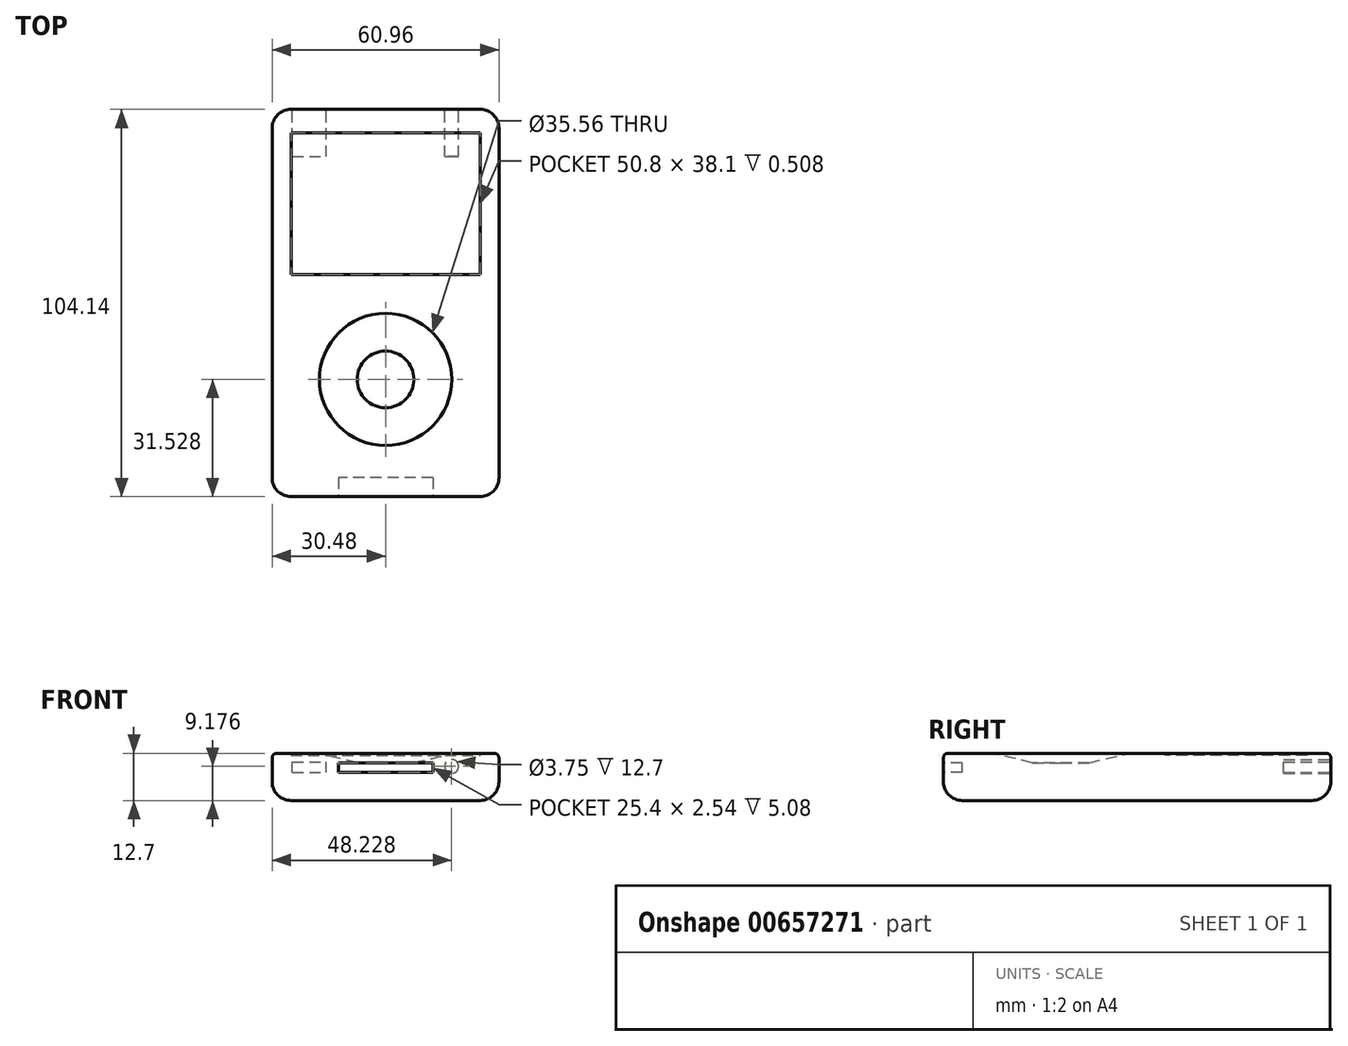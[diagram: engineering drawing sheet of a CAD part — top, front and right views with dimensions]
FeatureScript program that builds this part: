
annotation { "Feature Type Name" : "Feature", "Feature Type Description" : "" }
export const myFeature = defineFeature(function(context is Context, id is Id, definition is map)
    precondition{}
    {
        {
            var Q0;
            Q0=qCreatedBy(makeId("Top.planeOp"),FACE);
            var sketch = newSketch(context, id + "F0", { "sketchPlane" : qUnion([Q0])});
            skLineSegment(sketch, "E0.bottom", {"start": v(30.48, -52.07) * mm, "end": v(-30.48, -52.07) * mm});
            skLineSegment(sketch, "E0.top", {"start": v(30.48, 52.07) * mm, "end": v(-30.48, 52.07) * mm});
            skLineSegment(sketch, "E0.left", {"start": v(30.48, -52.07) * mm, "end": v(30.48, 52.07) * mm});
            skLineSegment(sketch, "E0.right", {"start": v(-30.48, -52.07) * mm, "end": v(-30.48, 52.07) * mm});
            skPoint(sketch, "E0.middle", {"position": v(0, 0) * mm});
            skCircle(sketch, "E1", {"center": v(0, -21.59) * mm, "radius": 17.78 * mm});
            skCircle(sketch, "E2", {"center": v(0, -21.59) * mm, "radius": 7.62 * mm});
            skLineSegment(sketch, "E3.bottom", {"start": v(-25.4, 45.72) * mm, "end": v(25.4, 45.72) * mm});
            skLineSegment(sketch, "E3.top", {"start": v(-25.4, 7.62) * mm, "end": v(25.4, 7.62) * mm});
            skLineSegment(sketch, "E3.left", {"start": v(-25.4, 45.72) * mm, "end": v(-25.4, 7.62) * mm});
            skLineSegment(sketch, "E3.right", {"start": v(25.4, 45.72) * mm, "end": v(25.4, 7.62) * mm});
            skPoint(sketch, "E3.middle", {"position": v(0, 26.67) * mm});
            skLineSegment(sketch, "E4", {"start": v(-30.48, -21.56) * mm, "end": v(30.48, -21.56) * mm, "construction": true});
            skSolve(sketch);
        }
        {
            var Q0;
            Q0=sQuery(id+"F0.wireOp",EDGE,"E0.bottom");
            cPlane(context, id + "F1", {"entities" : qUnion([Q0]), "cplaneType" : CPlaneType.LINE_ANGLE, "offset" : 25.4 * mm, "angle" : 0 * degree, "width" : 152.4 * mm, "height" : 152.4 * mm});
        }
        {
            var Q0;
            Q0=sQuery(id+"F0.wireOp",EDGE,"E0.top");
            cPlane(context, id + "F2", {"entities" : qUnion([Q0]), "cplaneType" : CPlaneType.LINE_ANGLE, "offset" : 25.4 * mm, "angle" : 0 * degree, "width" : 152.4 * mm, "height" : 152.4 * mm});
        }
        {
            var Q0;
            Q0=qCreatedBy(id+"F1.planeOp",FACE);
            var sketch = newSketch(context, id + "F3", { "sketchPlane" : qUnion([Q0])});
            skLineSegment(sketch, "E5.bottom", {"start": v(12.7, -5.08) * mm, "end": v(-12.7, -5.08) * mm});
            skLineSegment(sketch, "E5.top", {"start": v(12.7, -2.54) * mm, "end": v(-12.7, -2.54) * mm});
            skLineSegment(sketch, "E5.left", {"start": v(12.7, -5.08) * mm, "end": v(12.7, -2.54) * mm});
            skLineSegment(sketch, "E5.right", {"start": v(-12.7, -5.08) * mm, "end": v(-12.7, -2.54) * mm});
            skPoint(sketch, "E5.middle", {"position": v(0, -3.81) * mm});
            skSolve(sketch);
        }
        {
            var Q0;
            Q0=qCreatedBy(id+"F2.planeOp",FACE);
            var sketch = newSketch(context, id + "F4", { "sketchPlane" : qUnion([Q0])});
            skCircle(sketch, "E6", {"center": v(17.75, -3.52) * mm, "radius": 1.88 * mm});
            skLineSegment(sketch, "E7.bottom", {"start": v(-25.05, -5.18) * mm, "end": v(-15.9, -5.18) * mm});
            skLineSegment(sketch, "E7.top", {"start": v(-25.05, -2.38) * mm, "end": v(-15.9, -2.38) * mm});
            skLineSegment(sketch, "E7.left", {"start": v(-25.05, -5.18) * mm, "end": v(-25.05, -2.38) * mm});
            skLineSegment(sketch, "E7.right", {"start": v(-15.9, -5.18) * mm, "end": v(-15.9, -2.38) * mm});
            skPoint(sketch, "E7.middle", {"position": v(-20.48, -3.78) * mm});
            skSolve(sketch);
        }
        {
            var Q0;
            Q0=makeQuery(id+"F0.imprint","IMPRINT",FACE,{"disambiguationData":[TD([[makeQuery(id+"F0.imprint","IMPRINT",EDGE,{"derivedFrom":sQuery(id+"F0.wireOp",EDGE,"E0.bottom")}),-1.0]])]});
            var Q1;
            Q1=makeQuery(id+"F0.imprint","IMPRINT",FACE,{"disambiguationData":[TD([[makeQuery(id+"F0.imprint","IMPRINT",EDGE,{"derivedFrom":sQuery(id+"F0.wireOp",EDGE,"E3.bottom")}),-1.0]])]});
            var Q2;
            Q2=makeQuery(id+"F0.imprint","IMPRINT",FACE,{"disambiguationData":[TD([[makeQuery(id+"F0.imprint","IMPRINT",EDGE,{"derivedFrom":sQuery(id+"F0.wireOp",EDGE,"E1")}),1.0]])]});
            var Q3;
            Q3=makeQuery(id+"F0.imprint","IMPRINT",FACE,{"disambiguationData":[TD([[makeQuery(id+"F0.imprint","IMPRINT",EDGE,{"derivedFrom":sQuery(id+"F0.wireOp",EDGE,"E2")}),1.0]])]});
            extrude(context, id + "F5", {"entities" : qUnion([Q0, Q1, Q2, Q3]), "oppositeDirection" : true, "depth" : 12.7 * mm, "offsetDistance" : 25.4 * mm});
        }
        {
            var Q0;
            Q0=makeQuery(id+"F5.opExtrude","CAP_FACE",FACE,{"disambiguationData":[OSD([sQuery(id+"F0.wireOp",EDGE,"E0.bottom"),sQuery(id+"F0.wireOp",EDGE,"E0.top"),sQuery(id+"F0.wireOp",EDGE,"E0.left"),sQuery(id+"F0.wireOp",EDGE,"E0.right")])],"isStart":false});
            fillet(context, id + "F6", {"entities" : qUnion([Q0]), "radius" : 5.08 * mm, "tangentPropagation" : true, "allowEdgeOverflow" : false});
        }
        {
            var Q0;
            Q0=makeQuery(id+"F5.opExtrude","CAP_FACE",FACE,{"disambiguationData":[OSD([sQuery(id+"F0.wireOp",EDGE,"E0.bottom"),sQuery(id+"F0.wireOp",EDGE,"E0.top"),sQuery(id+"F0.wireOp",EDGE,"E0.left"),sQuery(id+"F0.wireOp",EDGE,"E0.right")])],"isStart":true});
            fillet(context, id + "F7", {"entities" : qUnion([Q0]), "radius" : 1.27 * mm, "tangentPropagation" : true, "allowEdgeOverflow" : false});
        }
        {
            var Q0;
            Q0=makeQuery(id+"F5.opExtrude","SWEPT_EDGE",EDGE,{"disambiguationData":[OSD([sQuery(id+"F0.wireOp",EDGE,"E0.bottom"),sQuery(id+"F0.wireOp",EDGE,"E0.right")])]});
            var Q1;
            Q1=makeQuery(id+"F7.opFillet","BLEND_EDGE",EDGE,{"blendedFrom":[makeQuery(id+"F5.opExtrude","CAP_EDGE",EDGE,{"disambiguationData":[OSD([sQuery(id+"F0.wireOp",EDGE,"E0.bottom")])],"isStart":true}),makeQuery(id+"F5.opExtrude","CAP_EDGE",EDGE,{"disambiguationData":[OSD([sQuery(id+"F0.wireOp",EDGE,"E0.right")])],"isStart":true})],"blendedInto":[]});
            var Q2;
            Q2=makeQuery(id+"F6.opFillet","BLEND_EDGE",EDGE,{"blendedFrom":[makeQuery(id+"F5.opExtrude","CAP_EDGE",EDGE,{"disambiguationData":[OSD([sQuery(id+"F0.wireOp",EDGE,"E0.bottom")])],"isStart":false}),makeQuery(id+"F5.opExtrude","CAP_EDGE",EDGE,{"disambiguationData":[OSD([sQuery(id+"F0.wireOp",EDGE,"E0.right")])],"isStart":false})],"blendedInto":[]});
            fillet(context, id + "F8", {"entities" : qUnion([Q0, Q1, Q2]), "radius" : 5.08 * mm, "tangentPropagation" : true, "allowEdgeOverflow" : false});
        }
        {
            var Q0;
            Q0=makeQuery(id+"F7.opFillet","BLEND_EDGE",EDGE,{"blendedFrom":[makeQuery(id+"F5.opExtrude","CAP_EDGE",EDGE,{"disambiguationData":[OSD([sQuery(id+"F0.wireOp",EDGE,"E0.bottom")])],"isStart":true}),makeQuery(id+"F5.opExtrude","CAP_EDGE",EDGE,{"disambiguationData":[OSD([sQuery(id+"F0.wireOp",EDGE,"E0.left")])],"isStart":true})],"blendedInto":[]});
            var Q1;
            Q1=makeQuery(id+"F5.opExtrude","SWEPT_EDGE",EDGE,{"disambiguationData":[OSD([sQuery(id+"F0.wireOp",EDGE,"E0.bottom"),sQuery(id+"F0.wireOp",EDGE,"E0.left")])]});
            var Q2;
            Q2=makeQuery(id+"F6.opFillet","BLEND_EDGE",EDGE,{"blendedFrom":[makeQuery(id+"F5.opExtrude","CAP_EDGE",EDGE,{"disambiguationData":[OSD([sQuery(id+"F0.wireOp",EDGE,"E0.bottom")])],"isStart":false}),makeQuery(id+"F5.opExtrude","CAP_EDGE",EDGE,{"disambiguationData":[OSD([sQuery(id+"F0.wireOp",EDGE,"E0.left")])],"isStart":false})],"blendedInto":[]});
            fillet(context, id + "F9", {"entities" : qUnion([Q0, Q1, Q2]), "radius" : 5.08 * mm, "tangentPropagation" : true, "allowEdgeOverflow" : false});
        }
        {
            var Q0;
            Q0=makeQuery(id+"F7.opFillet","BLEND_EDGE",EDGE,{"blendedFrom":[makeQuery(id+"F5.opExtrude","CAP_EDGE",EDGE,{"disambiguationData":[OSD([sQuery(id+"F0.wireOp",EDGE,"E0.top")])],"isStart":true}),makeQuery(id+"F5.opExtrude","CAP_EDGE",EDGE,{"disambiguationData":[OSD([sQuery(id+"F0.wireOp",EDGE,"E0.left")])],"isStart":true})],"blendedInto":[]});
            var Q1;
            Q1=makeQuery(id+"F5.opExtrude","SWEPT_EDGE",EDGE,{"disambiguationData":[OSD([sQuery(id+"F0.wireOp",EDGE,"E0.top"),sQuery(id+"F0.wireOp",EDGE,"E0.left")])]});
            var Q2;
            Q2=makeQuery(id+"F6.opFillet","BLEND_EDGE",EDGE,{"blendedFrom":[makeQuery(id+"F5.opExtrude","CAP_EDGE",EDGE,{"disambiguationData":[OSD([sQuery(id+"F0.wireOp",EDGE,"E0.top")])],"isStart":false}),makeQuery(id+"F5.opExtrude","CAP_EDGE",EDGE,{"disambiguationData":[OSD([sQuery(id+"F0.wireOp",EDGE,"E0.left")])],"isStart":false})],"blendedInto":[]});
            fillet(context, id + "F10", {"entities" : qUnion([Q0, Q1, Q2]), "radius" : 5.08 * mm, "tangentPropagation" : true, "allowEdgeOverflow" : false});
        }
        {
            var Q0;
            Q0=makeQuery(id+"F7.opFillet","BLEND_EDGE",EDGE,{"blendedFrom":[makeQuery(id+"F5.opExtrude","CAP_EDGE",EDGE,{"disambiguationData":[OSD([sQuery(id+"F0.wireOp",EDGE,"E0.top")])],"isStart":true}),makeQuery(id+"F5.opExtrude","CAP_EDGE",EDGE,{"disambiguationData":[OSD([sQuery(id+"F0.wireOp",EDGE,"E0.right")])],"isStart":true})],"blendedInto":[]});
            var Q1;
            Q1=makeQuery(id+"F5.opExtrude","SWEPT_EDGE",EDGE,{"disambiguationData":[OSD([sQuery(id+"F0.wireOp",EDGE,"E0.top"),sQuery(id+"F0.wireOp",EDGE,"E0.right")])]});
            var Q2;
            Q2=makeQuery(id+"F6.opFillet","BLEND_EDGE",EDGE,{"blendedFrom":[makeQuery(id+"F5.opExtrude","CAP_EDGE",EDGE,{"disambiguationData":[OSD([sQuery(id+"F0.wireOp",EDGE,"E0.top")])],"isStart":false}),makeQuery(id+"F5.opExtrude","CAP_EDGE",EDGE,{"disambiguationData":[OSD([sQuery(id+"F0.wireOp",EDGE,"E0.right")])],"isStart":false})],"blendedInto":[]});
            fillet(context, id + "F11", {"entities" : qUnion([Q0, Q1, Q2]), "radius" : 5.08 * mm, "tangentPropagation" : true, "allowEdgeOverflow" : false});
        }
        {
            var Q0;
            Q0=makeQuery(id+"F3.imprint","IMPRINT",FACE,{"disambiguationData":[TD([[makeQuery(id+"F3.imprint","IMPRINT",EDGE,{"derivedFrom":sQuery(id+"F3.wireOp",EDGE,"E5.bottom")}),-1.0]])]});
            extrude(context, id + "F12", {"entities" : qUnion([Q0]), "operationType" : NewBodyOperationType.REMOVE, "oppositeDirection" : true, "depth" : 5.08 * mm, "offsetDistance" : 25.4 * mm});
        }
        {
            var Q0;
            Q0=makeQuery(id+"F4.imprint","IMPRINT",FACE,{"disambiguationData":[TD([[makeQuery(id+"F4.imprint","IMPRINT",EDGE,{"derivedFrom":sQuery(id+"F4.wireOp",EDGE,"E7.bottom")}),1.0]])]});
            extrude(context, id + "F13", {"entities" : qUnion([Q0]), "operationType" : NewBodyOperationType.REMOVE, "depth" : 1.27 * mm, "offsetDistance" : 25.4 * mm});
        }
        {
            var Q0;
            Q0 = qSketchRegion(id + "F4", true);
            extrude(context, id + "F14", {"entities" : qUnion([Q0]), "operationType" : NewBodyOperationType.REMOVE, "depth" : 12.7 * mm, "offsetDistance" : 25.4 * mm});
        }
        {
            var Q0;
            Q0=qCreatedBy(makeId("Right.planeOp"),FACE);
            var sketch = newSketch(context, id + "F15", { "sketchPlane" : qUnion([Q0])});
            skLineSegment(sketch, "E8", {"start": v(-38.32, 4.5) * mm, "end": v(-38.32, -0.13) * mm});
            skLineSegment(sketch, "E9", {"start": v(-38.32, -0.13) * mm, "end": v(-28.16, -2.54) * mm});
            skLineSegment(sketch, "E10", {"start": v(-28.16, -2.54) * mm, "end": v(-20.54, -2.54) * mm});
            skLineSegment(sketch, "E11", {"start": v(-20.54, -2.54) * mm, "end": v(-20.54, 5.24) * mm});
            skLineSegment(sketch, "E12", {"start": v(-20.54, 5.24) * mm, "end": v(-38.32, 4.5) * mm});
            skSolve(sketch);
        }
        {
            var Q0;
            Q0=makeQuery(id+"F15.imprint","IMPRINT",FACE,{"disambiguationData":[TD([[makeQuery(id+"F15.imprint","IMPRINT",EDGE,{"derivedFrom":sQuery(id+"F15.wireOp",EDGE,"E8")}),1.0]])]});
            var Q1;
            Q1=sQuery(id+"F15.wireOp",EDGE,"E11");
            revolve(context, id + "F16", {"operationType" : NewBodyOperationType.REMOVE, "entities" : qUnion([Q0]), "axis" : qUnion([Q1]), "revolveType" : RevolveType.FULL, "oppositeDirection" : true});
        }
        {
            var Q0;
            Q0=makeQuery(id+"F0.imprint","IMPRINT",FACE,{"disambiguationData":[TD([[makeQuery(id+"F0.imprint","IMPRINT",EDGE,{"derivedFrom":sQuery(id+"F0.wireOp",EDGE,"E3.bottom")}),-1.0]])]});
            extrude(context, id + "F17", {"entities" : qUnion([Q0]), "operationType" : NewBodyOperationType.REMOVE, "oppositeDirection" : true, "depth" : 0.5 * mm, "offsetDistance" : 25.4 * mm});
        }
    });
